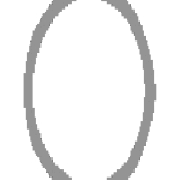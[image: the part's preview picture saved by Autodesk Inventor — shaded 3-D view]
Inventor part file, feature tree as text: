
AUTODESK INVENTOR PART (.ipt)
format: ipt  version: 2021 (Build 250183000, 183)  size: 113,152 bytes
history: native  units: in
note: dims shown in document units (in); Inventor stores cm internally (conversion verified against a paired STEP export)
features: other x4, sketch x3, plane x1
ambient origin geometry x8: Origin, YZ Plane, XZ Plane, XY Plane, X Axis, Y Axis, Z Axis, Center Point
bodies: Solid1 (feature_tree), Body (feature_tree)
feature tree (8):
  other  "Driven Length"
  other  "Frame Generator"
  other  "Start Plane"
  other  "End Plane"
  sketch  "Sketch"  dims[d2=3.5in d4=-0.0in d5=3.5in d6=0.12in d7=0.0in d8=90.0deg d9=3.5in]
  sketch  "Sketch2"  dims[d0=1.0in]
  plane  "Work Plane3"
  sketch  "Sketch3"  dims[d1=0.065in]
